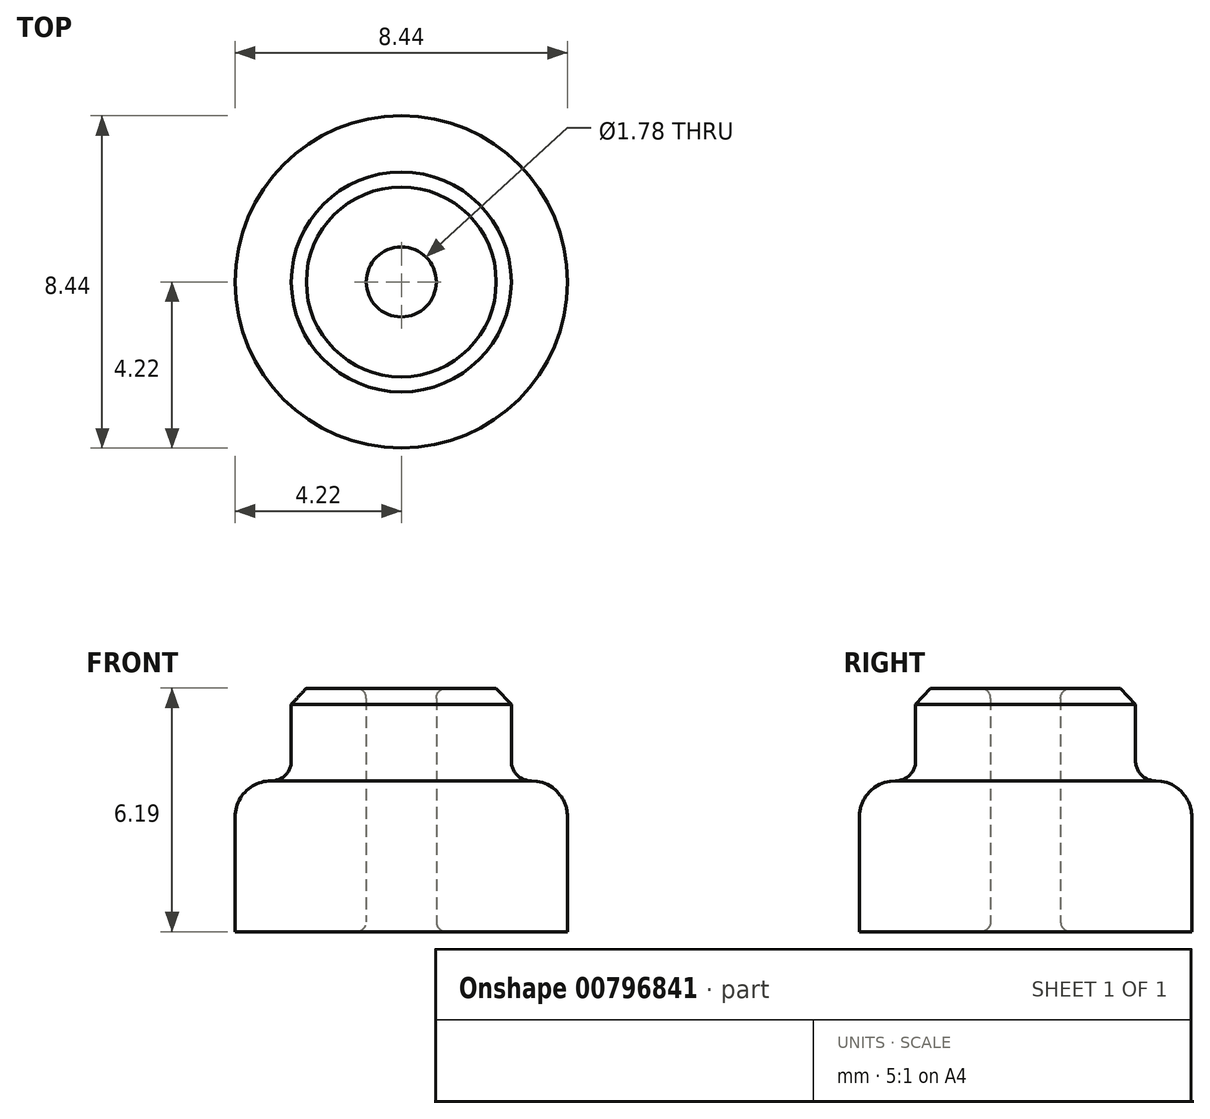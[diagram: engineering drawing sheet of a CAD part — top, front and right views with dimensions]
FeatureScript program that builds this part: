
annotation { "Feature Type Name" : "Feature", "Feature Type Description" : "" }
export const myFeature = defineFeature(function(context is Context, id is Id, definition is map)
    precondition{}
    {
        {
            var Q0;
            Q0=qCreatedBy(makeId("Right.planeOp"),FACE);
            var sketch = newSketch(context, id + "F0", { "sketchPlane" : qUnion([Q0])});
            skLineSegment(sketch, "E0", {"start": v(0, 0) * mm, "end": v(0, 6.35) * mm});
            skLineSegment(sketch, "E1.0", {"start": v(-0.89, 0.25) * mm, "end": v(-0.89, 5.93) * mm});
            skLineSegment(sketch, "E2", {"start": v(-1.14, 6.19) * mm, "end": v(-2.41, 6.19) * mm});
            skLineSegment(sketch, "E3", {"start": v(-2.8, 5.78) * mm, "end": v(-2.8, 4.34) * mm});
            skLineSegment(sketch, "E4", {"start": v(-4.22, 0) * mm, "end": v(-1.14, 0) * mm});
            skLineSegment(sketch, "E5.0", {"start": v(-3.3, 3.83) * mm, "end": v(-3.3, 3.83) * mm});
            skLineSegment(sketch, "E6", {"start": v(-2.8, 5.78) * mm, "end": v(-2.41, 6.19) * mm});
            skArc(sketch, "E7.filletArc", {"start": v(-3.3, 3.83) * mm, "mid": v(-2.94, 3.98) * mm, "end": v(-2.8, 4.34) * mm});
            skLineSegment(sketch, "E8.0", {"start": v(-4.22, 2.92) * mm, "end": v(-4.22, 0) * mm});
            skArc(sketch, "E9.filletArc", {"start": v(-3.3, 3.83) * mm, "mid": v(-3.95, 3.56) * mm, "end": v(-4.22, 2.92) * mm});
            skArc(sketch, "E10.filletArc", {"start": v(-0.89, 5.93) * mm, "mid": v(-0.96, 6.11) * mm, "end": v(-1.14, 6.19) * mm});
            skArc(sketch, "E11.filletArc", {"start": v(-1.14, 0) * mm, "mid": v(-0.96, 0.07) * mm, "end": v(-0.89, 0.25) * mm});
            skSolve(sketch);
        }
        {
            var Q0;
            Q0 = qSketchRegion(id + "F0", true);
            var Q1;
            Q1=sQuery(id+"F0.wireOp",EDGE,"E0");
            revolve(context, id + "F1", {"surfaceOperationType" : NewSurfaceOperationType.NEW, "entities" : qUnion([Q0]), "axis" : qUnion([Q1]), "revolveType" : RevolveType.FULL});
        }
    });
